# Revit family: ROTHOB_Rothoblaas_FallProtection_AOS01
name_source: partatom
category: Collegamenti strutturali
units: mm (PartAtom-declared; Revit-internal decimal feet)

## family parameters
Attiva taglio nelle viste = Sì
Condiviso = No
Host = Superficie
Materiale per comportamento modello = Acciaio
Numero OmniClass = 23.27.71.21
Taglio con vuoti quando caricato = No
Titolo OmniClass = Fall Arrest Systems

## types (1)
- 60x98mm
    AssetType = Fixed
    BIMObjectName = ROTHOB_Rothoblaas_FallProtection_AOS01
    Category = Pr_40_70_75_75 - Safety access anchor devices
    CodePerformance = Safety system
    Color = Silver
    Constituents = Plate, fastening (threaded rod, nuts, bolts, washers)
    Description = Anchor point
    DurationUnit = Years
    Esporta tipo in formato IFC con nome = IfcBuildingElementProxyType
    Features = Anchor point
    IfcExportAs = IfcBuildingElementProxyType
    IfcExportType = USERDEFINED
    Length_L = 98 mm
    ManufacturerName = ROTHO BLAAS SRL
    ManufacturerURL = www.rothoblaas.com
    Material = AISI 304 stainless steel grade 1.4301
    MinWeight = 0.257 kg
    ModelDisclaimer = The latest version of the data sheets can be found on our website
    ModelNumber = AOS01
    Name = Anchor point
    NominalLength = 98 mm
    NominalWidth = 60 mm
    ObjectMaterial = ROTHOB_Rothoblaas_StainlessSteel
    OmniClassCode = 23-27 71 21
    OmniClassTitle = Fall Arrest Systems
    OmniClassVersion = 2012-05-16
    ProductInformation = https://www.rothoblaas.com
    Prospetto di default = 1219.2 mm  [stored 4 ft]
    ReferenceStandard = EN 795:2012 A
    Shape = Three-dimensional
    Size = 60x98 mm
    Tipo IFC predefinito = USERDEFINED
    UniClass2015Code = Pr_40_70_75_75
    UniClass2015Title = Safety access anchor devices
    UniClass2015Version = Products v1.30
    Version = 2
    Width_B = 60 mm

note: [stored X ft] marks values corroborated as IEEE doubles in the binary element streams (Revit-internal decimal feet)
